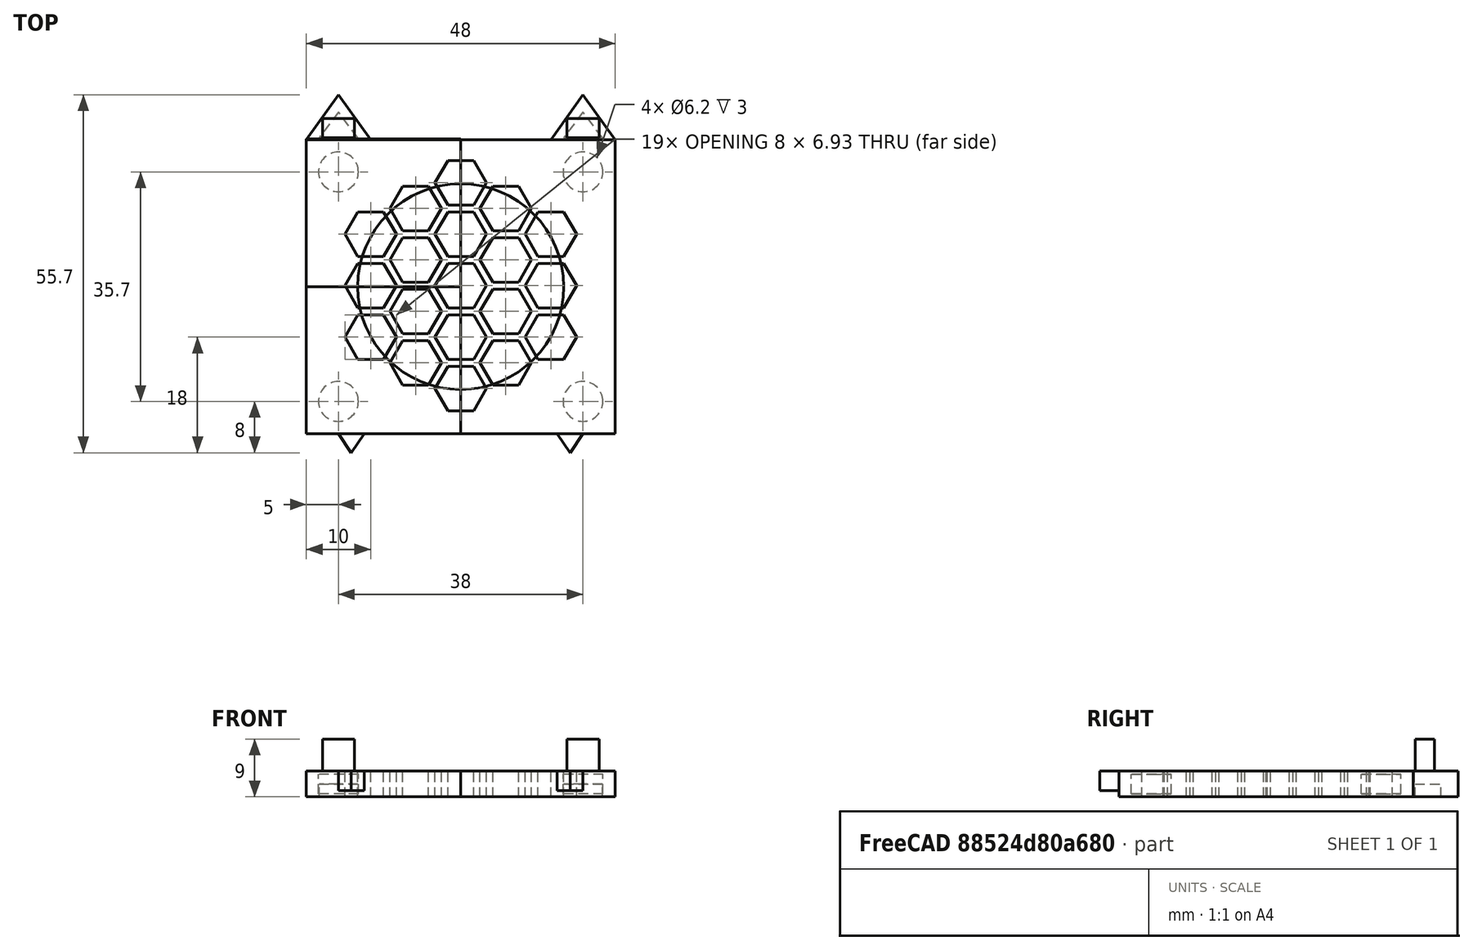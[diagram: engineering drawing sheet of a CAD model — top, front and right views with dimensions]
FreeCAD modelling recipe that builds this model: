
FCSTD DOCUMENT  (FreeCAD 0.18R14555 (Git shallow))
Label: fan-cover
License: All rights reserved
LicenseURL: http://en.wikipedia.org/wiki/All_rights_reserved
objects: Part::Feature×20, Part::MultiFuse×8, Part::Box×6, Part::Cylinder×5, Part::Cut×4
note: 43 computed .brp shape members not serialized (recipe doc carries the construction recipe); baked Part::Feature solids carry a one-line shape summary decoded from their .brp

FEATURE [Part::Box] Box  label="Cube"
  AttacherType = Attacher::AttachEngine3D
  Height = 4
  Length = 48
  Width = 45.7
FEATURE [Part::Box] Box001  label="Cube001"
  AttacherType = Attacher::AttachEngine3D
  Height = 4
  Length = 24
  Width = 22.85
FEATURE [Part::Cylinder] Cylinder
  Angle = 360
  AttacherType = Attacher::AttachEngine3D
  Height = 4
  Placement = pos=(24,22.85,0) rot=(0,0,1;0rad)
  Radius = 16
FEATURE [Part::Cylinder] Cylinder001
  Angle = 360
  AttacherType = Attacher::AttachEngine3D
  Height = 3
  Placement = pos=(5,5,0) rot=(0,0,1;0rad)
  Radius = 3.1
FEATURE [Part::Cylinder] Cylinder002
  Angle = 360
  AttacherType = Attacher::AttachEngine3D
  Height = 3
  Placement = pos=(43,40.7,0) rot=(0,0,1;0rad)
  Radius = 3.1
FEATURE [Part::Cylinder] Cylinder003
  Angle = 360
  AttacherType = Attacher::AttachEngine3D
  Height = 3
  Placement = pos=(5,40.7,0) rot=(0,0,1;0rad)
  Radius = 3.1
FEATURE [Part::Cylinder] Cylinder004
  Angle = 360
  AttacherType = Attacher::AttachEngine3D
  Height = 3
  Placement = pos=(43,5,0) rot=(0,0,1;0rad)
  Radius = 3.1
FEATURE [Part::MultiFuse] Fusion
  Placement = pos=(0,0,0.5) rot=(0,0,1;0rad)
  Shapes = -> [Cylinder003,Cylinder002,Cylinder004,Cylinder001]
FEATURE [Part::Box] Box002  label="Cube002"
  AttacherType = Attacher::AttachEngine3D
  Height = 4
  Length = 24
  Width = 45.85
FEATURE [Part::Feature] Body001
  Placement = pos=(22,42,0) rot=(0,0,1;0rad)
  shape: bbox 8 x 6.928 x 4 mm, 8 faces (baked)
FEATURE [Part::Feature] Body002
  Placement = pos=(22,34,0) rot=(0,0,1;0rad)
  shape: bbox 8 x 6.928 x 4 mm, 8 faces (baked)
FEATURE [Part::Feature] Body003
  Placement = pos=(22,26,0) rot=(0,0,1;0rad)
  shape: bbox 8 x 6.928 x 4 mm, 8 faces (baked)
FEATURE [Part::Feature] Body004
  Placement = pos=(22,18,0) rot=(0,0,1;0rad)
  shape: bbox 8 x 6.928 x 4 mm, 8 faces (baked)
FEATURE [Part::Feature] Body005
  Placement = pos=(22,10,0) rot=(0,0,1;0rad)
  shape: bbox 8 x 6.928 x 4 mm, 8 faces (baked)
FEATURE [Part::Feature] Body006
  Placement = pos=(29,14,0) rot=(0,0,1;0rad)
  shape: bbox 8 x 6.928 x 4 mm, 8 faces (baked)
FEATURE [Part::Feature] Body007
  Placement = pos=(29,22,0) rot=(0,0,1;0rad)
  shape: bbox 8 x 6.928 x 4 mm, 8 faces (baked)
FEATURE [Part::Feature] Body008
  Placement = pos=(29,30,0) rot=(0,0,1;0rad)
  shape: bbox 8 x 6.928 x 4 mm, 8 faces (baked)
FEATURE [Part::Feature] Body009
  Placement = pos=(29,38,0) rot=(0,0,1;0rad)
  shape: bbox 8 x 6.928 x 4 mm, 8 faces (baked)
FEATURE [Part::Feature] Body010
  Placement = pos=(36,34,0) rot=(0,0,1;0rad)
  shape: bbox 8 x 6.928 x 4 mm, 8 faces (baked)
FEATURE [Part::Feature] Body011
  Placement = pos=(36,26,0) rot=(0,0,1;0rad)
  shape: bbox 8 x 6.928 x 4 mm, 8 faces (baked)
FEATURE [Part::Feature] Body012
  Placement = pos=(36,18,0) rot=(0,0,1;0rad)
  shape: bbox 8 x 6.928 x 4 mm, 8 faces (baked)
FEATURE [Part::MultiFuse] Fusion001
  Shapes = -> [Body012,Body011,Body010]
FEATURE [Part::MultiFuse] Fusion002
  Shapes = -> [Body009,Body008,Body007,Body006]
FEATURE [Part::MultiFuse] Fusion003
  Shapes = -> [Body005,Body004,Body003,Body002,Body001]
FEATURE [Part::Feature] Fusion002001  label="Fusion004"
  Placement = pos=(-14,0,0) rot=(0,0,1;0rad)
  shape: bbox 8 x 30.93 x 4 mm, 32 faces, 4 solids (baked)
FEATURE [Part::Feature] Fusion001001  label="Fusion005"
  Placement = pos=(-28,0,0) rot=(0,0,1;0rad)
  shape: bbox 8 x 22.93 x 4 mm, 24 faces, 3 solids (baked)
FEATURE [Part::MultiFuse] Fusion002002
  Placement = pos=(0,1,0) rot=(0,0,1;0rad)
  Shapes = -> [Fusion002001,Fusion002,Fusion001001,Fusion001,Fusion003]
FEATURE [Part::Cut] Cut
  Base = -> Box
  Tool = -> Fusion002002
FEATURE [Part::Cut] Cut001
  Base = -> Cut
  Tool = -> Fusion
FEATURE [Part::Feature] Body013
  Placement = pos=(-2,-8.3,0) rot=(0,0,1;0rad)
  shape: bbox 10 x 7 x 4 mm, 5 faces (baked)
FEATURE [Part::Feature] Body014
  Placement = pos=(36,-8.3,0) rot=(0,0,1;0rad)
  shape: bbox 10 x 7 x 4 mm, 5 faces (baked)
FEATURE [Part::Box] Box003  label="Cube003"
  AttacherType = Attacher::AttachEngine3D
  Height = 5
  Length = 5
  Placement = pos=(2.5,46,4) rot=(0,0,1;0rad)
  Width = 3
FEATURE [Part::Box] Box004  label="Cube004"
  AttacherType = Attacher::AttachEngine3D
  Height = 5
  Length = 5
  Placement = pos=(40.5,46,4) rot=(0,0,1;0rad)
  Width = 3
FEATURE [Part::Feature] Body015
  Placement = pos=(-3,2,0) rot=(0,0,1;0rad)
  shape: bbox 4 x 3 x 4 mm, 5 faces (baked)
FEATURE [Part::Feature] Body016
  Placement = pos=(31,2,0) rot=(0,0,1;0rad)
  shape: bbox 4 x 3 x 4 mm, 5 faces (baked)
FEATURE [Part::Feature] Body017
  Placement = pos=(21,40,0) rot=(0,0,1;0rad)
  shape: bbox 6 x 4 x 2 mm, 5 faces (baked)
FEATURE [Part::Feature] Body018
  Placement = pos=(59,40,0) rot=(0,0,1;0rad)
  shape: bbox 6 x 4 x 2 mm, 5 faces (baked)
FEATURE [Part::MultiFuse] Fusion002003
  Shapes = -> [Body018,Body017]
FEATURE [Part::MultiFuse] Fusion002004
  Shapes = -> [Body014,Body013]
FEATURE [Part::Cut] Cut002
  Base = -> Fusion002004
  Tool = -> Fusion002003
FEATURE [Part::Box] Box005  label="Cube005"
  AttacherType = Attacher::AttachEngine3D
  Height = 1
  Length = 48
  Placement = pos=(0,-3,0) rot=(0,0,1;0rad)
  Width = 3
FEATURE [Part::MultiFuse] Fusion002005
  Shapes = -> [Body016,Body015]
FEATURE [Part::Cut] Cut003
  Base = -> Fusion002005
  Tool = -> Box005
